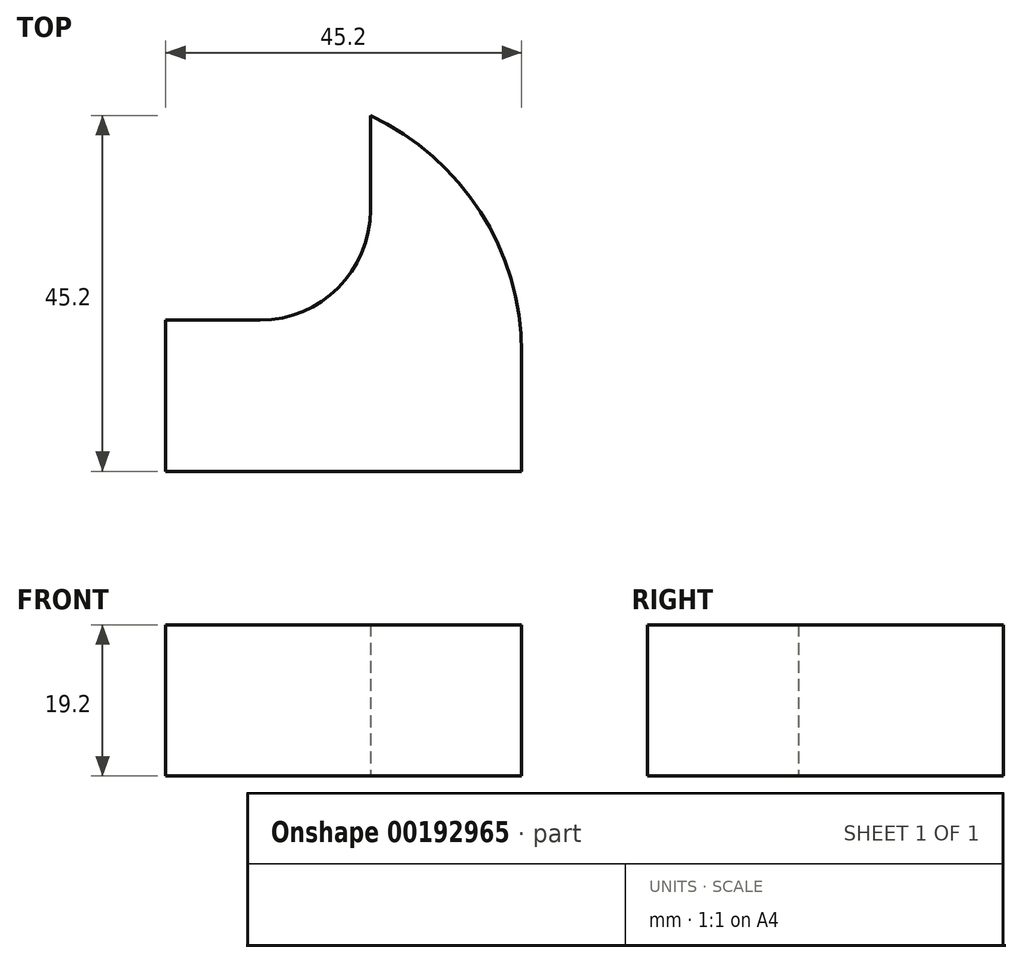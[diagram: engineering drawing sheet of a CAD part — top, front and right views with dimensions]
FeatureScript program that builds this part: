
annotation { "Feature Type Name" : "Feature", "Feature Type Description" : "" }
export const myFeature = defineFeature(function(context is Context, id is Id, definition is map)
    precondition{}
    {
        {
            var Q0;
            Q0=qCreatedBy(makeId("Top.planeOp"),FACE);
            var sketch = newSketch(context, id + "F0", { "sketchPlane" : qUnion([Q0])});
            skLineSegment(sketch, "E0.bottom", {"start": v(22.6, -9.6) * mm, "end": v(-22.6, -9.6) * mm});
            skLineSegment(sketch, "E0.top", {"start": v(22.6, 9.6) * mm, "end": v(-22.6, 9.6) * mm});
            skLineSegment(sketch, "E0.left", {"start": v(22.6, -9.6) * mm, "end": v(22.6, 9.6) * mm});
            skLineSegment(sketch, "E0.right", {"start": v(-22.6, -9.6) * mm, "end": v(-22.6, 9.6) * mm});
            skPoint(sketch, "E0.middle", {"position": v(0, 0) * mm});
            skLineSegment(sketch, "E1.bottom", {"start": v(22.6, -9.6) * mm, "end": v(3.4, -9.6) * mm});
            skLineSegment(sketch, "E1.top", {"start": v(22.6, 35.6) * mm, "end": v(3.4, 35.6) * mm});
            skLineSegment(sketch, "E1.left", {"start": v(22.6, -9.6) * mm, "end": v(22.6, 35.6) * mm});
            skLineSegment(sketch, "E1.right", {"start": v(3.4, -9.6) * mm, "end": v(3.4, 35.6) * mm});
            skSolve(sketch);
        }
        {
            var Q0;
            Q0 = qSketchRegion(id + "F0", true);
            extrude(context, id + "F1", {"entities" : qUnion([Q0]), "depth" : 19.2 * mm});
        }
        {
            var Q0;
            Q0=makeQuery(id+"F1.opExtrude","SWEPT_EDGE",EDGE,{"disambiguationData":[OSD([sQuery(id+"F0.wireOp",EDGE,"E0.top"),sQuery(id+"F0.wireOp",EDGE,"E1.right")])]});
            fillet(context, id + "F2", {"entities" : qUnion([Q0]), "radius" : 14 * mm, "tangentPropagation" : true, "allowEdgeOverflow" : false});
        }
        {
            var Q0;
            Q0=makeQuery(id+"F1.opExtrude","SWEPT_EDGE",EDGE,{"disambiguationData":[OSD([sQuery(id+"F0.wireOp",EDGE,"E1.bottom"),sQuery(id+"F0.wireOp",EDGE,"E1.left")])]});
            fillet(context, id + "F3", {"entities" : qUnion([Q0]), "radius" : (14 + 19.2) * mm, "tangentPropagation" : true, "allowEdgeOverflow" : false});
        }
    });
